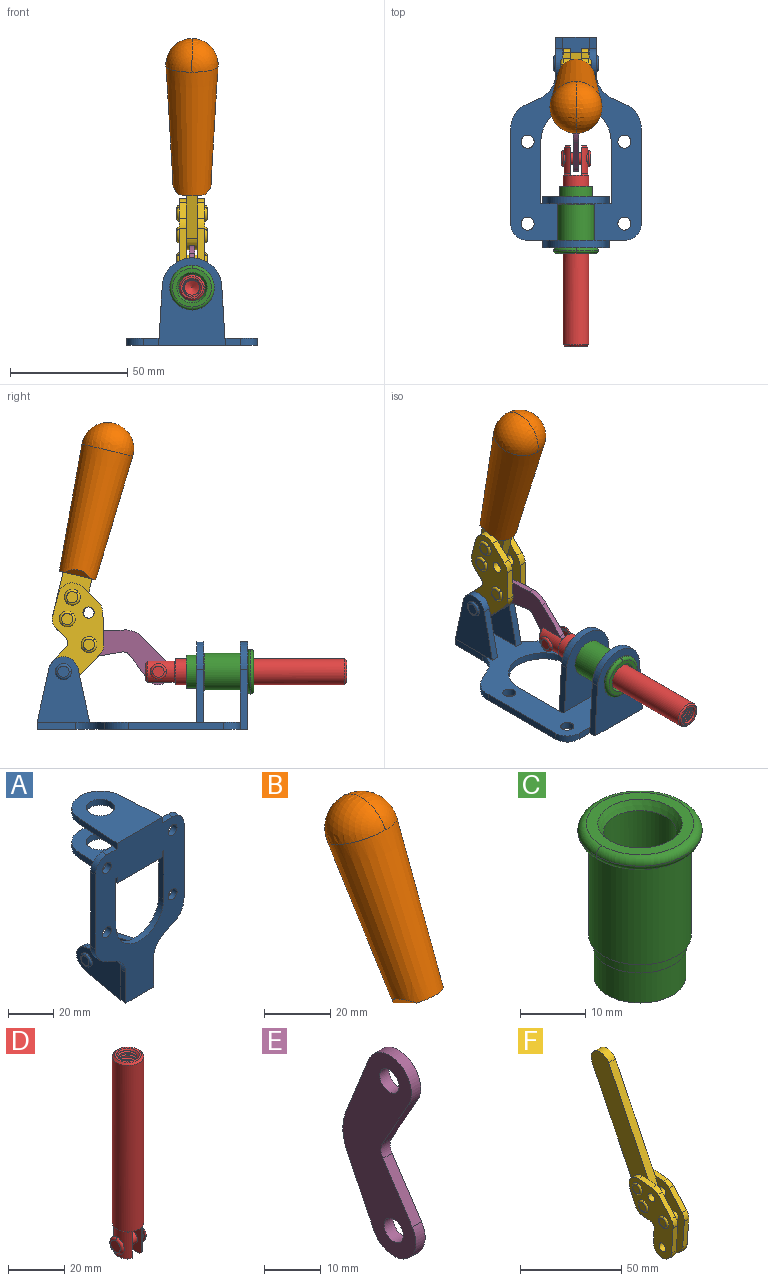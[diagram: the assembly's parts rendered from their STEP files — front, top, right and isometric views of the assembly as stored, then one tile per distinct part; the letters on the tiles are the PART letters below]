
ASSEMBLY  parts=6 mates=6
PART A: 55 faces, bbox 55.7x37.4x89.8 mm
  f0: torus R=2.41mm, axis (-1,0,0), area 15mm2, adj f11,f15,f25
  f1: torus R=2.41mm, axis (-1,0,0), area 15mm2, adj f10,f12,f22
  f2: cylinder r=2.78mm len=5.56mm, axis (0,-1,0), area 54.2mm2, adj f30,f54
  f3: cylinder r=14.99mm len=29.97mm, axis (0,-1,0), area 145.9mm2, adj f30,f49,f53,f54
  f4: cylinder r=2.78mm len=5.56mm, axis (0,-1,0), area 54.2mm2, adj f30,f54
  f5: cylinder r=2.78mm len=5.56mm, axis (0,-1,0), area 54.2mm2, adj f30,f54
  f6: cylinder r=2.78mm len=5.56mm, axis (0,-1,0), area 54.2mm2, adj f30,f54
  f7: cylinder r=6.35mm len=12.7mm, axis (0,0,1), area 123.6mm2, adj f27,f51
  f8: cylinder r=6.35mm len=12.7mm, axis (0,0,-1), area 124.7mm2, adj f21,f35
  f9: cylinder r=2.41mm len=11.18mm, axis (-1,0,0), area 169.4mm2, adj f16,f19
  f10: plane 4.83x4.83mm, normal (1,0,0), area 18.3mm2, adj f1,f12
  f11: plane 4.83x4.83mm, normal (-1,0,0), area 18.3mm2, adj f0,f15
  f12: torus R=2.41mm, axis (-1,0,0), area 15mm2, adj f1,f10,f22
  f13: cylinder r=6.35mm len=12.41mm, axis (1,0,0), area 53.4mm2, adj f18,f19,f22,f23
  f14: cylinder r=6.35mm len=12.41mm, axis (-1,0,0), area 53.4mm2, adj f16,f17,f24,f25
  f15: torus R=2.41mm, axis (-1,0,0), area 15mm2, adj f0,f11,f25
  f16: plane 27.86x22.35mm, normal (1,0,0), area 425.4mm2, adj f9,f14,f17,f24,f30
  f17: plane 22.86x4.97mm, normal (0,0.21,0.98), area 72.5mm2, adj f14,f16,f25,f30
  f18: plane 22.86x4.97mm, normal (0,0.21,0.98), area 72.5mm2, adj f13,f19,f22,f30
  f19: plane 27.86x22.35mm, normal (-1,0,0), area 425.4mm2, adj f9,f13,f18,f23,f30
  f20: cylinder r=12.7mm len=25.35mm, axis (0,0,-1), area 119.8mm2, adj f21,f34,f35,f36
  f21: plane 34.21x28.07mm, normal (0,0,-1), area 702.4mm2, adj f8,f20,f30,f34,f36
  f22: plane 27.96x22.45mm, normal (1,0,0), area 407.2mm2, adj f1,f12,f13,f18,f23,f30,f42,f43
  f23: plane 22.86x4.97mm, normal (0,0.21,-0.98), area 72.5mm2, adj f13,f19,f22,f44
  f24: plane 22.86x4.97mm, normal (0,0.21,-0.98), area 72.5mm2, adj f14,f16,f25,f44
  f25: plane 27.86x22.35mm, normal (-1,0,0), area 407.1mm2, adj f0,f14,f15,f17,f24,f30,f45,f46
  f26: plane 3.1x0.95mm, normal (0,0,-1), area 2.7mm2, adj f30,f49,f50,f54
  f27: plane 34.21x28.07mm, normal (0,0,1), area 702.4mm2, adj f7,f28,f30,f50,f52
  f28: cylinder r=12.7mm len=25.35mm, axis (0,0,1), area 118.8mm2, adj f27,f50,f51,f52
  f29: plane 3.1x0.95mm, normal (0,0,-1), area 2.7mm2, adj f30,f52,f53,f54
  f30: plane 86.54x55.63mm, normal (0,1,0), area 2362.9mm2, adj f2,f3,f4,f5,f6,f16,f17,f18
  f31: plane 40.56x3.1mm, normal (-1,0,0), area 125.7mm2, adj f30,f32,f48,f54
  f32: cylinder r=7.11mm len=7.11mm, axis (0,-1,0), area 34.6mm2, adj f30,f31,f33,f54
  f33: plane 6.67x3.1mm, normal (0,0,1), area 20.4mm2, adj f30,f32,f34,f54
  f34: plane 25.39x3.13mm, normal (-1,0.06,0), area 79.5mm2, adj f20,f21,f33,f35,f54
  f35: plane 37.31x28.45mm, normal (0,0,1), area 789.9mm2, adj f8,f20,f34,f36,f54
  f36: plane 25.39x3.13mm, normal (1,0.06,0), area 79.5mm2, adj f20,f21,f35,f37,f54
  f37: plane 6.67x3.1mm, normal (0,0,1), area 20.4mm2, adj f30,f36,f38,f54
  f38: cylinder r=7.11mm len=7.11mm, axis (0,-1,0), area 34.6mm2, adj f30,f37,f39,f54
  f39: plane 40.56x3.1mm, normal (1,0,0), area 125.7mm2, adj f30,f38,f40,f54
  f40: cylinder r=11.18mm len=10.16mm, axis (0,-1,0), area 39.5mm2, adj f30,f39,f41,f54
  f41: plane 6.09x3.1mm, normal (0.42,0,-0.91), area 20.8mm2, adj f30,f40,f42,f54
  f42: cylinder r=11.18mm len=9.41mm, axis (0,-1,0), area 37.2mm2, adj f22,f30,f41,f43,f54
  f43: plane 16.5x3.1mm, normal (1,0,0), area 51.1mm2, adj f22,f42,f44,f54
  f44: plane 17.37x3.1mm, normal (0,0,-1), area 53.8mm2, adj f23,f24,f30,f43,f45,f54
  f45: plane 16.5x3.1mm, normal (-1,0,0), area 51.1mm2, adj f25,f44,f46,f54
  f46: cylinder r=11.18mm len=9.41mm, axis (0,-1,0), area 37.2mm2, adj f25,f30,f45,f47,f54
  f47: plane 6.09x3.1mm, normal (-0.42,0,-0.91), area 20.8mm2, adj f30,f46,f48,f54
  f48: cylinder r=11.18mm len=10.16mm, axis (0,-1,0), area 39.5mm2, adj f30,f31,f47,f54
  f49: plane 26.54x3.1mm, normal (-1,0,0), area 82.3mm2, adj f3,f26,f30,f54
  f50: plane 25.39x3.1mm, normal (1,0.06,0), area 78.8mm2, adj f26,f27,f28,f51,f54
  f51: plane 37.31x28.45mm, normal (0,0,-1), area 789.9mm2, adj f7,f28,f50,f52,f54
  f52: plane 25.39x3.1mm, normal (-1,0.06,0), area 78.8mm2, adj f27,f28,f29,f51,f54
  f53: plane 26.54x3.1mm, normal (1,0,0), area 82.3mm2, adj f3,f29,f30,f54
  f54: plane 89.66x55.63mm, normal (0,-1,0), area 2678.5mm2, adj f2,f3,f4,f5,f6,f26,f29,f31
PART B: 11 faces, bbox 22.3x42.6x64.5 mm
  f0: sphere r=11.13mm, area 411.4mm2, adj f1,f8
  f1: cone r=11.11mm half-angle=3.3deg, axis (0,0.44,0.9), area 3251.8mm2, adj f0,f7,f8,f9,f10
  f2: cylinder r=6.16mm len=11.7mm, axis (1,0,0), area 89.5mm2, adj f3,f4,f5,f6
  f3: plane 60.23x36.75mm, normal (-1,0,0), area 763.6mm2, adj f2,f4,f6,f10
  f4: plane 51.37x25.05mm, normal (0,0.9,-0.44), area 264.2mm2, adj f2,f3,f5,f10
  f5: plane 60.23x36.75mm, normal (1,0,0), area 763.6mm2, adj f2,f4,f6,f10
  f6: plane 51.37x25.05mm, normal (0,-0.9,0.44), area 264.2mm2, adj f2,f3,f5,f10
  f7: plane 9.95x5.95mm, normal (0.71,-0.31,-0.64), area 25.8mm2, adj f1,f10
  f8: sphere r=11.13mm, area 411.4mm2, adj f0,f1
  f9: plane 9.95x5.95mm, normal (-0.71,-0.31,-0.64), area 25.8mm2, adj f1,f10
  f10: plane 14.27x11.38mm, normal (0,-0.44,-0.9), area 106.7mm2, adj f1,f3,f4,f5,f6,f7,f9
PART C: 15 faces, bbox 20.6x20.6x28.7 mm
  f0: torus R=8.26mm, axis (0,0,1), area 56.8mm2, adj f1,f10,f12
  f1: torus R=8.26mm, axis (0,0,1), area 56.8mm2, adj f0,f6,f13
  f2: cylinder r=5.59mm len=25.91mm, axis (0,0,1), area 909.6mm2, adj f3,f4
  f3: cone r=6.86mm half-angle=45deg, axis (0,0,-1), area 70.2mm2, adj f2,f14
  f4: cone r=6.47mm half-angle=30deg, axis (0,0,1), area 66.7mm2, adj f2,f13
  f5: cylinder r=7.04mm len=14.07mm, axis (0,0,1), area 252.6mm2, adj f11,f14
  f6: torus R=8.26mm, axis (0,0,1), area 56.8mm2, adj f1,f12,f13
  f7: cylinder r=7.16mm len=14.33mm, axis (0,0,1), area 91.5mm2, adj f9,f11
  f8: cylinder r=7.86mm len=18.42mm, axis (0,0,1), area 909.6mm2, adj f9,f10
  f9: plane 15.72x15.72mm, normal (0,0,-1), area 33mm2, adj f7,f8
  f10: plane 16.51x16.51mm, normal (0,0,-1), area 19.9mm2, adj f0,f8,f12
  f11: plane 14.33x14.33mm, normal (0,0,-1), area 5.7mm2, adj f5,f7
  f12: torus R=8.26mm, axis (0,0,1), area 56.8mm2, adj f0,f6,f10
  f13: plane 16.51x16.51mm, normal (0,0,1), area 82.7mm2, adj f1,f4,f6
  f14: plane 14.07x14.07mm, normal (0,0,-1), area 7.8mm2, adj f3,f5
PART D: 48 faces, bbox 12.6x11.1x86.1 mm
  f0: torus R=2.41mm, axis (-1,0,0), area 15mm2, adj f30,f32,f34
  f1: torus R=2.41mm, axis (-1,0,0), area 15mm2, adj f29,f31,f33
  f2: cylinder r=5.54mm len=72.39mm, axis (0,0,1), area 2518.5mm2, adj f3,f4,f42,f43
  f3: cone r=5.54mm half-angle=45deg, axis (0,0,1), area 7.6mm2, adj f2,f5,f41
  f4: cone r=5.54mm half-angle=45deg, axis (0,0,-1), area 34.9mm2, adj f2,f39
  f5: cylinder r=5.08mm len=11.48mm, axis (0,0,1), area 108.3mm2, adj f3,f7,f8,f41
  f6: cylinder r=2.41mm len=4.83mm, axis (-1,0,0), area 71.2mm2, adj f40,f41
  f7: cylinder r=2.41mm len=4.83mm, axis (-1,0,0), area 7.6mm2, adj f5,f34
  f8: cone r=5.08mm half-angle=45deg, axis (0,0,1), area 10.6mm2, adj f5,f37,f41
  f9: cone r=3.98mm half-angle=45deg, axis (0,0,1), area 17.6mm2, adj f27,f39,f45,f46,f47
  f10: cylinder r=2.41mm len=4.83mm, axis (-1,0,0), area 7.6mm2, adj f33,f38
  f11: cylinder r=3.2mm len=6.4mm, axis (0,0,1), area 78.4mm2, adj f12,f28,f44,f45,f47
  f12: cylinder r=3.2mm len=6.4mm, axis (0,0,1), area 10.5mm2, adj f11,f13,f45,f47
  f13: cylinder r=3.2mm len=6.4mm, axis (0,0,1), area 10.5mm2, adj f12,f14,f45,f47
  f14: cylinder r=3.2mm len=6.4mm, axis (0,0,1), area 10.5mm2, adj f13,f15,f45,f47
  f15: cylinder r=3.2mm len=6.4mm, axis (0,0,1), area 10.5mm2, adj f14,f16,f45,f47
  f16: cylinder r=3.2mm len=6.4mm, axis (0,0,1), area 10.5mm2, adj f15,f17,f45,f47
  f17: cylinder r=3.2mm len=6.4mm, axis (0,0,1), area 10.5mm2, adj f16,f18,f45,f47
  f18: cylinder r=3.2mm len=6.4mm, axis (0,0,1), area 10.5mm2, adj f17,f19,f45,f47
  f19: cylinder r=3.2mm len=6.4mm, axis (0,0,1), area 10.5mm2, adj f18,f20,f45,f47
  f20: cylinder r=3.2mm len=6.4mm, axis (0,0,1), area 10.5mm2, adj f19,f21,f45,f47
  f21: cylinder r=3.2mm len=6.4mm, axis (0,0,1), area 10.5mm2, adj f20,f22,f45,f47
  f22: cylinder r=3.2mm len=6.4mm, axis (0,0,1), area 10.5mm2, adj f21,f23,f45,f47
  f23: cylinder r=3.2mm len=6.4mm, axis (0,0,1), area 10.5mm2, adj f22,f24,f45,f47
  f24: cylinder r=3.2mm len=6.4mm, axis (0,0,1), area 10.5mm2, adj f23,f25,f45,f47
  f25: cylinder r=3.2mm len=6.4mm, axis (0,0,1), area 10.5mm2, adj f24,f26,f45,f47
  f26: cylinder r=3.2mm len=6.4mm, axis (0,0,1), area 10.5mm2, adj f25,f27,f45,f47
  f27: cylinder r=3.2mm len=6.4mm, axis (0,0,1), area 7.4mm2, adj f9,f26,f45,f47
  f28: cone r=3.2mm half-angle=60deg, axis (0,0,1), area 37.2mm2, adj f11
  f29: plane 4.83x4.83mm, normal (-1,0,0), area 18.3mm2, adj f1,f31
  f30: plane 4.83x4.83mm, normal (1,0,0), area 18.3mm2, adj f0,f32
  f31: torus R=2.41mm, axis (-1,0,0), area 15mm2, adj f1,f29,f33
  f32: torus R=2.41mm, axis (-1,0,0), area 15mm2, adj f0,f30,f34
  f33: plane 6.83x6.83mm, normal (1,0,0), area 18.3mm2, adj f1,f10,f31
  f34: plane 6.83x6.83mm, normal (-1,0,0), area 18.3mm2, adj f0,f7,f32
  f35: cone r=5.08mm half-angle=45deg, axis (0,0,1), area 10.6mm2, adj f36,f38,f40
  f36: plane 7.25x1.97mm, normal (0,0,-1), area 10mm2, adj f35,f40
  f37: plane 7.25x1.97mm, normal (0,0,-1), area 10mm2, adj f8,f41
  f38: cylinder r=5.08mm len=11.48mm, axis (0,0,1), area 108.3mm2, adj f10,f35,f40,f42
  f39: plane 9.55x9.55mm, normal (0,0,1), area 22mm2, adj f4,f9
  f40: plane 12.76x10.09mm, normal (1,0,0), area 95.7mm2, adj f6,f35,f36,f38,f42,f43
  f41: plane 12.76x10.09mm, normal (-1,0,0), area 95.7mm2, adj f3,f5,f6,f8,f37,f43
  f42: cone r=5.54mm half-angle=45deg, axis (0,0,1), area 7.6mm2, adj f2,f38,f40
  f43: plane 11.07x4.7mm, normal (0,0,-1), area 50.4mm2, adj f2,f40,f41
  f44: plane 0.89x0.62mm, normal (-1,0,0), area 0.3mm2, adj f11,f45,f46,f47
  f45: bspline ~24.8x7.63mm, area 266.6mm2, adj f9,f11,f12,f13,f14,f15,f16,f17
  f46: bspline ~24.87x7.63mm, area 73.6mm2, adj f9,f44,f45,f47
  f47: bspline ~24.98x7.63mm, area 272.5mm2, adj f9,f11,f12,f13,f14,f15,f16,f17
PART E: 12 faces, bbox 2.3x18.2x42.8 mm
  f0: cylinder r=2.4mm len=4.8mm, axis (1,0,0), area 34.9mm2, adj f4,f11
  f1: cylinder r=10.41mm len=8.47mm, axis (1,0,0), area 20.2mm2, adj f4,f9,f10,f11
  f2: cylinder r=3.05mm len=3.16mm, axis (1,0,0), area 7.7mm2, adj f4,f6,f7,f11
  f3: cylinder r=2.4mm len=4.8mm, axis (1,0,0), area 34.9mm2, adj f4,f11
  f4: plane 42.81x18.23mm, normal (-1,0,0), area 414.1mm2, adj f0,f1,f2,f3,f5,f6,f7,f8
  f5: cylinder r=5.54mm len=10.67mm, axis (1,0,0), area 41.8mm2, adj f4,f6,f10,f11
  f6: plane 11.66x6.53mm, normal (0,-0.87,-0.49), area 30.9mm2, adj f2,f4,f5,f11
  f7: plane 11.17x7.33mm, normal (0,-0.84,0.55), area 30.9mm2, adj f2,f4,f8,f11
  f8: cylinder r=5.54mm len=10.51mm, axis (1,0,0), area 41.8mm2, adj f4,f7,f9,f11
  f9: plane 13.67x6.67mm, normal (0,0.9,-0.44), area 35.1mm2, adj f1,f4,f8,f11
  f10: plane 14.1x5.7mm, normal (0,0.93,0.37), area 35.1mm2, adj f1,f4,f5,f11
  f11: plane 42.81x18.23mm, normal (1,0,0), area 414.1mm2, adj f0,f1,f2,f3,f5,f6,f7,f8
PART F: 59 faces, bbox 12.9x60.2x99.6 mm
  f0: torus R=2.39mm, axis (-1,0,0), area 14.9mm2, adj f20,f43,f51
  f1: torus R=2.39mm, axis (-1,0,0), area 14.9mm2, adj f19,f42,f51
  f2: torus R=2.39mm, axis (-1,0,0), area 14.9mm2, adj f18,f35,f51
  f3: torus R=2.39mm, axis (-1,0,0), area 14.9mm2, adj f14,f17,f23
  f4: torus R=2.39mm, axis (-1,0,0), area 14.9mm2, adj f13,f16,f23
  f5: torus R=2.39mm, axis (-1,0,0), area 14.9mm2, adj f12,f15,f23
  f6: cylinder r=2.39mm len=4.78mm, axis (1,0,0), area 46.5mm2, adj f48,f50,f51
  f7: cylinder r=2.39mm len=4.78mm, axis (1,0,0), area 46.5mm2, adj f50,f51
  f8: cylinder r=6.35mm len=12.68mm, axis (1,0,0), area 61.8mm2, adj f38,f39,f50,f51
  f9: cylinder r=2.39mm len=4.78mm, axis (-1,0,0), area 70.5mm2, adj f46,f50
  f10: cylinder r=2.39mm len=4.78mm, axis (-1,0,0), area 46.5mm2, adj f23,f45,f46
  f11: cylinder r=2.39mm len=4.78mm, axis (-1,0,0), area 46.5mm2, adj f23,f46
  f12: plane 4.78x4.78mm, normal (1,0,0), area 17.9mm2, adj f5,f15
  f13: plane 4.78x4.78mm, normal (1,0,0), area 17.9mm2, adj f4,f16
  f14: plane 4.78x4.78mm, normal (1,0,0), area 17.9mm2, adj f3,f17
  f15: torus R=2.39mm, axis (-1,0,0), area 14.9mm2, adj f5,f12,f23
  f16: torus R=2.39mm, axis (-1,0,0), area 14.9mm2, adj f4,f13,f23
  f17: torus R=2.39mm, axis (-1,0,0), area 14.9mm2, adj f3,f14,f23
  f18: plane 4.78x4.78mm, normal (-1,0,0), area 17.9mm2, adj f2,f35
  f19: plane 4.78x4.78mm, normal (-1,0,0), area 17.9mm2, adj f1,f42
  f20: plane 4.78x4.78mm, normal (-1,0,0), area 17.9mm2, adj f0,f43
  f21: plane 2.26x0.2mm, normal (1,0,0), area 0.2mm2, adj f31,f44
  f22: plane 2.26x0.2mm, normal (-1,0,0), area 0.2mm2, adj f41,f44
  f23: plane 39.37x30.77mm, normal (1,0,0), area 565.5mm2, adj f3,f4,f5,f10,f11,f15,f16,f17
  f24: cylinder r=6.1mm len=4.15mm, axis (-1,0,0), area 14.7mm2, adj f23,f25,f32,f46
  f25: plane 10.25x9.01mm, normal (0,-0.75,0.66), area 42.3mm2, adj f23,f24,f26,f46
  f26: cylinder r=6.35mm len=4.64mm, axis (-1,0,0), area 15.6mm2, adj f23,f25,f27,f46
  f27: plane 15.84x3.1mm, normal (0,-1,-0.07), area 49.2mm2, adj f23,f26,f28,f46
  f28: cylinder r=6.35mm len=12.68mm, axis (-1,0,0), area 61.8mm2, adj f23,f27,f29,f46
  f29: plane 8.11x3.1mm, normal (0,1,0.07), area 25.2mm2, adj f23,f28,f30,f46
  f30: cylinder r=3.05mm len=3.25mm, axis (-1,0,0), area 14.8mm2, adj f23,f29,f31,f46
  f31: plane 5.99x3.1mm, normal (0,0.07,-1), area 18.6mm2, adj f21,f23,f30,f44,f46
  f32: plane 9.5x3.1mm, normal (0,-0.07,1), area 29.5mm2, adj f23,f24,f33,f46,f47
  f33: cylinder r=6.1mm len=8.63mm, axis (-1,0,0), area 39.1mm2, adj f23,f32,f34,f47
  f34: plane 8.65x3.96mm, normal (0,0.91,-0.42), area 29.5mm2, adj f23,f33,f44,f47
  f35: torus R=2.39mm, axis (-1,0,0), area 14.9mm2, adj f2,f18,f51
  f36: plane 10.25x9.01mm, normal (0,-0.75,0.66), area 42.3mm2, adj f37,f49,f50,f51
  f37: cylinder r=6.35mm len=4.64mm, axis (1,0,0), area 15.6mm2, adj f36,f38,f50,f51
  f38: plane 15.84x3.1mm, normal (0,-1,-0.07), area 49.2mm2, adj f8,f37,f50,f51
  f39: plane 8.11x3.1mm, normal (0,1,0.07), area 25.2mm2, adj f8,f40,f50,f51
  f40: cylinder r=3.05mm len=3.25mm, axis (1,0,0), area 14.8mm2, adj f39,f41,f50,f51
  f41: plane 5.99x3.1mm, normal (0,0.07,-1), area 18.6mm2, adj f22,f40,f44,f50,f51
  f42: torus R=2.39mm, axis (-1,0,0), area 14.9mm2, adj f1,f19,f51
  f43: torus R=2.39mm, axis (-1,0,0), area 14.9mm2, adj f0,f20,f51
  f44: cylinder r=6.35mm len=12.12mm, axis (-1,0,0), area 128.9mm2, adj f21,f22,f23,f31,f34,f41,f46,f47
  f45: plane 2.65x1.35mm, normal (1,0,0), area 1mm2, adj f10,f55
  f46: plane 39.08x20.42mm, normal (-1,0,0), area 412.5mm2, adj f9,f10,f11,f24,f25,f26,f27,f28
  f47: plane 77.62x39.82mm, normal (1,0,0), area 850mm2, adj f32,f33,f34,f44,f53,f54,f55
  f48: plane 2.65x1.35mm, normal (-1,0,0), area 1mm2, adj f6,f55
  f49: cylinder r=6.1mm len=4.15mm, axis (1,0,0), area 14.7mm2, adj f36,f50,f51,f56
  f50: plane 39.08x20.42mm, normal (1,0,0), area 412.5mm2, adj f6,f7,f8,f9,f36,f37,f38,f39
  f51: plane 39.37x30.77mm, normal (-1,0,0), area 565.5mm2, adj f0,f1,f2,f6,f7,f8,f35,f36
  f52: plane 8.65x3.96mm, normal (0,0.91,-0.42), area 29.5mm2, adj f44,f51,f57,f58
  f53: plane 68.49x33.4mm, normal (0,0.9,-0.44), area 358.1mm2, adj f44,f47,f54,f58
  f54: cylinder r=6.35mm len=12.06mm, axis (1,0,0), area 93.7mm2, adj f47,f53,f55,f58
  f55: plane 68.49x33.4mm, normal (0,-0.9,0.44), area 358.1mm2, adj f44,f45,f46,f47,f48,f50,f54,f58
  f56: plane 9.5x3.1mm, normal (0,-0.07,1), area 29.5mm2, adj f49,f50,f51,f57,f58
  f57: cylinder r=6.1mm len=8.63mm, axis (1,0,0), area 39.1mm2, adj f51,f52,f56,f58
  f58: plane 77.62x39.82mm, normal (-1,0,0), area 850mm2, adj f44,f52,f53,f54,f55,f56,f57
PLACE A rot(axis=(1,0,0),90deg) t=(-0.46,7.95,0.11)mm fixed
PLACE B rot(axis=(1,0,0),39.4deg) t=(-0.46,0.65,33.91)mm
PLACE C rot(axis=(0.58,-0.58,0.58),120deg) t=(24.16,7.95,24.72)mm
PLACE D rot(axis=(1,0,0),90deg) t=(-0.46,15.03,0.11)mm
PLACE E rot(axis=(1,0,0),113.3deg) t=(-0.46,23.51,8.24)mm
PLACE F rot(axis=(1,0,0),39.4deg) t=(-0.46,0.65,33.91)mm
MATE revolute D.f6 <-> E.f5  axis (-1,0,0) through (-0.46,-0.44,24.72)mm
MATE fastened C.f2 <-> A.f7  axis (0,-1,0) through (-0.46,-38.45,24.72)mm
MATE slider A.f7 <-> D.f2  axis (0,-1,0) through (-0.46,-38.45,24.72)mm
MATE revolute F.f7 <-> A.f0  axis (-1,0,0) through (-0.46,40.04,24.72)mm
MATE revolute F.f4 <-> E.f3  axis (-1,0,0) through (-0.46,29.14,36.26)mm
MATE fastened F.f54 <-> B.f2  axis (1,0,0) through (-0.46,20.81,121.32)mm
